# Revit family: 1030052(n0300)
name_source: partatom
category: Security Devices
units: mm (PartAtom-declared; Revit-internal decimal feet)

## family parameters
Always vertical = No
Cut with Voids When Loaded = No
Host = Ceiling
OmniClass Number = 23.85.30.14
OmniClass Title = Presence Detection/Registration
Room Calculation Point = No
Shared = Yes

## types (2) — shared parameters
zero-valued in all types: A

## per-type parameters (varying)
- Type 1: CTN=0; EF000008=0 mm  [stored 0 ft]; EF000040=0 mm  [stored 0 ft]; EF000049=0 mm  [stored 0 ft]; EF000194=0; EF000218=0 mm  [stored 0 ft]; EF000551=0 mm  [stored 0 ft]; EF000846=0 mm  [stored 0 ft]; EF001322=0 mm  [stored 0 ft]; EF001323=0 mm  [stored 0 ft]; EF003843=0 mm  [stored 0 ft]; EF003882=0; EF004101=0.00°; EF004265=0 mm  [stored 0 ft]; EF006589=0; EF006590=0; EF008011=0 mm  [stored 0 ft]; EF010886=0 mm  [stored 0 ft]; EF010945=0 mm  [stored 0 ft]; EF010946=0 mm  [stored 0 ft]; EF012278=0 mm  [stored 0 ft]; EF012569=0; LOG=0; NOCUPEROU=0; PRICEQUANTITY=0; QUANTITYINT=0; QUANTITYMIN=0
- 1030052: ARTICLENO=NB; BOMINFO=LINA; CATALOG=Theben; COO=CN; CTN=85365080; DEEPLINK_PRODUKTSEITE=http://www.theben.de; DESCLONG=Passive infrared presence detector for flush or surface ceiling mounting, Circular detection area 360°, Diameter 12 m, (113 square meters) at 3 m mounting height (transverse walking), Diameter 5 m, (20 square meters) at 3 m mounting height (sitting), 1 channel light (relay 230 V), Can also be used in damp rooms and outdoors due to protection class IP 54 (detection area outdoors 8 meters diameter), Can be remote controlled, Parallel connection with other LUXA 103 or theMura Slave possible, Switching capacity optimized for LED up to 400 W, Semi- or fully automatic operation, Integrated push button input, With pulse function, teach-in function, test function and staircase lighting function, Area restriction possible with cover clips, Housing color white; DESCSHORT=Presence detector ceiling mounting UP/DE, detection range 12 m, 1 x light; EF000003=EV000383; EF000007=White; EF000008=80 mm  [stored 0.262467 ft]; EF000010=Presence detector; EF000025=true; EF000040=62 mm  [stored 0.203412 ft]; EF000049=80 mm  [stored 0.262467 ft]; EF000124=Plug-in clamp; EF000139=Untreated; EF000147=false; EF000187=AC; EF000194=15; EF000218=48 mm  [stored 0.15748 ft]; EF000416=50, 50 Hz; EF000483=false; EF000551=80 mm  [stored 0.262467 ft]; EF000846=40 mm  [stored 0.131234 ft]; EF001098=true; EF001099=true; EF001198=false; EF001257=Thermoplast; EF001322=6000 mm  [stored 19.685 ft]; EF001323=6000 mm  [stored 19.685 ft]; EF001731=-25, 55 °C; EF002169=Plastic; EF003429=true; EF003808=false; EF003814=5, 1000 lx; EF003832=false; EF003843=113000 mm; EF003848=true; EF003858=false; EF003863=false; EF003876=true; EF003882=9010; EF003890=true; EF003898=true; EF003904=true; EF003920=false; EF004101=360.00°; EF004265=40 mm  [stored 0.131234 ft]; EF004293=IK04; EF005474=IP54; EF005624=false; EF006243=false; EF006311=false; EF006569=matt; EF006582=0, 360 °; EF006589=15; EF006590=30; EF006644=false; EF007575=true; EF008011=3000 mm; EF009569=false; EF010886=14 mm  [stored 0.0459318 ft]; EF010945=80 mm  [stored 0.262467 ft]; EF010946=60 mm  [stored 0.19685 ft]; EF011072=false; EF011991=false; EF012278=61 mm  [stored 0.200131 ft]; EF012569=50; EF014925=false; EF014926=false; EF014927=false; EF020270=Passive infrared; EF021180=true; EF023790=false; GEBRAUCHSANLEITUNG=http://www.theben.de; INTNO=4003468101735; LINA=1030052; LOG=300; MANUID=1030052; MANUNAME=Theben AG; MANUTYPEDESC=LUXA 103 S360-100-12 DE-UP WH; Manufacturer=Theben; Model=1030052; NB=1030052(N0300); NBSYN=$MANUID.($SA.$A.$LOG.); NN=LUXA 103; NOCUPEROU=1; PRICEQUANTITY=1; PRODUKTDATENBLATT=http://www.theben.de; QUANTITYINT=1; QUANTITYMIN=1; REACH_ERKLAERUNG=http://www.theben.de; REMARKS=ERP-GROUP 450; SA=None; SUPPLIER=THEBEN; SUPPLIERALTNO=1030052

note: [stored X ft] marks values corroborated as IEEE doubles in the binary element streams (Revit-internal decimal feet)

## geometry (parser evidence)
native form markers: Sweep x12
no freeform markers — native parametric forms only
